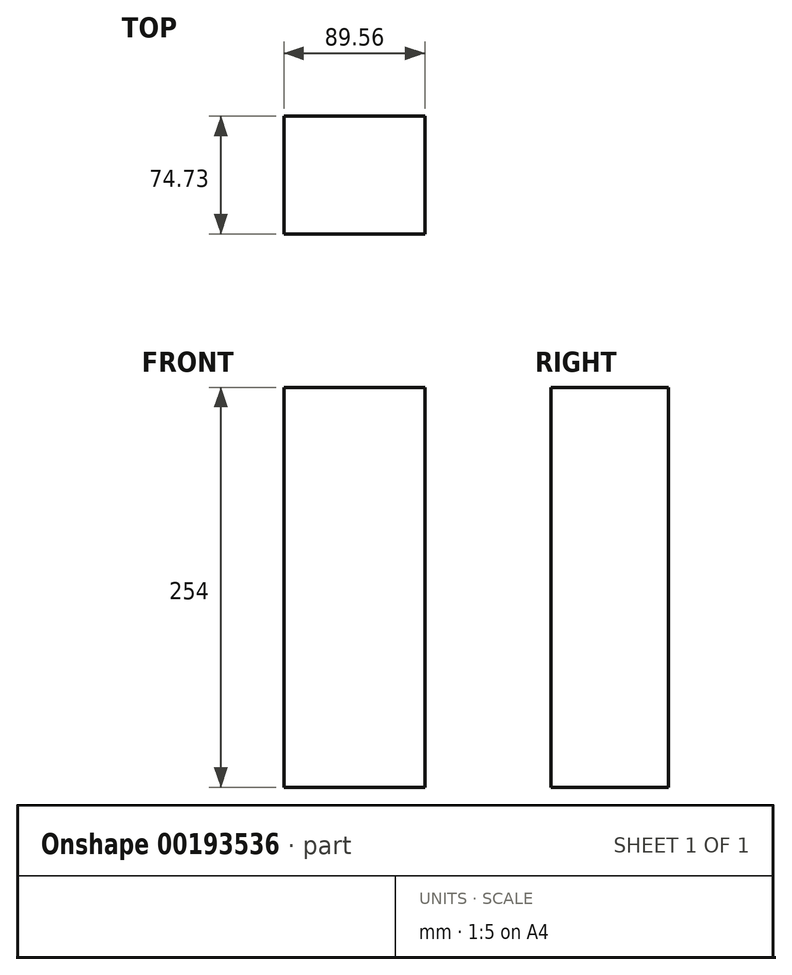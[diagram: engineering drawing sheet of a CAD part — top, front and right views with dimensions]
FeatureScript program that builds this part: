
annotation { "Feature Type Name" : "Feature", "Feature Type Description" : "" }
export const myFeature = defineFeature(function(context is Context, id is Id, definition is map)
    precondition{}
    {
        {
            var Q0;
            Q0=qCreatedBy(makeId("Top.planeOp"),FACE);
            var sketch = newSketch(context, id + "F0", { "sketchPlane" : qUnion([Q0])});
            skLineSegment(sketch, "E0.bottom", {"start": v(-36.51, 38.65) * mm, "end": v(53.05, 38.65) * mm});
            skLineSegment(sketch, "E0.top", {"start": v(-36.51, -36.08) * mm, "end": v(53.05, -36.08) * mm});
            skLineSegment(sketch, "E0.left", {"start": v(-36.51, 38.65) * mm, "end": v(-36.51, -36.08) * mm});
            skLineSegment(sketch, "E0.right", {"start": v(53.05, 38.65) * mm, "end": v(53.05, -36.08) * mm});
            skSolve(sketch);
        }
        {
            var Q0;
            Q0=makeQuery(id+"F0.imprint","IMPRINT",FACE,{"disambiguationData":[TD([[makeQuery(id+"F0.imprint","IMPRINT",EDGE,{"derivedFrom":sQuery(id+"F0.wireOp",EDGE,"E0.bottom")}),-1.0]])]});
            extrude(context, id + "F1", {"entities" : qUnion([Q0]), "depth" : 254 * mm});
        }
        {
            var Q0;
            Q0=qCreatedBy(makeId("Top.planeOp"),FACE);
            var sketch = newSketch(context, id + "F2", { "sketchPlane" : qUnion([Q0])});
            skLineSegment(sketch, "E1.bottom", {"start": v(23.39, 13.83) * mm, "end": v(-23.39, 13.83) * mm});
            skLineSegment(sketch, "E1.top", {"start": v(23.39, -26.1) * mm, "end": v(-23.39, -26.1) * mm});
            skLineSegment(sketch, "E1.left", {"start": v(23.39, 13.83) * mm, "end": v(23.39, -26.1) * mm});
            skLineSegment(sketch, "E1.right", {"start": v(-23.39, 13.83) * mm, "end": v(-23.39, -26.1) * mm});
            skPoint(sketch, "E1.middle", {"position": v(0, -6.13) * mm});
            skSolve(sketch);
        }
        {
            var Q0;
            Q0 = qSketchRegion(id + "F2", true);
            extrude(context, id + "F3", {"entities" : qUnion([Q0]), "operationType" : NewBodyOperationType.REMOVE, "oppositeDirection" : true, "depth" : 76.2 * mm});
        }
    });
